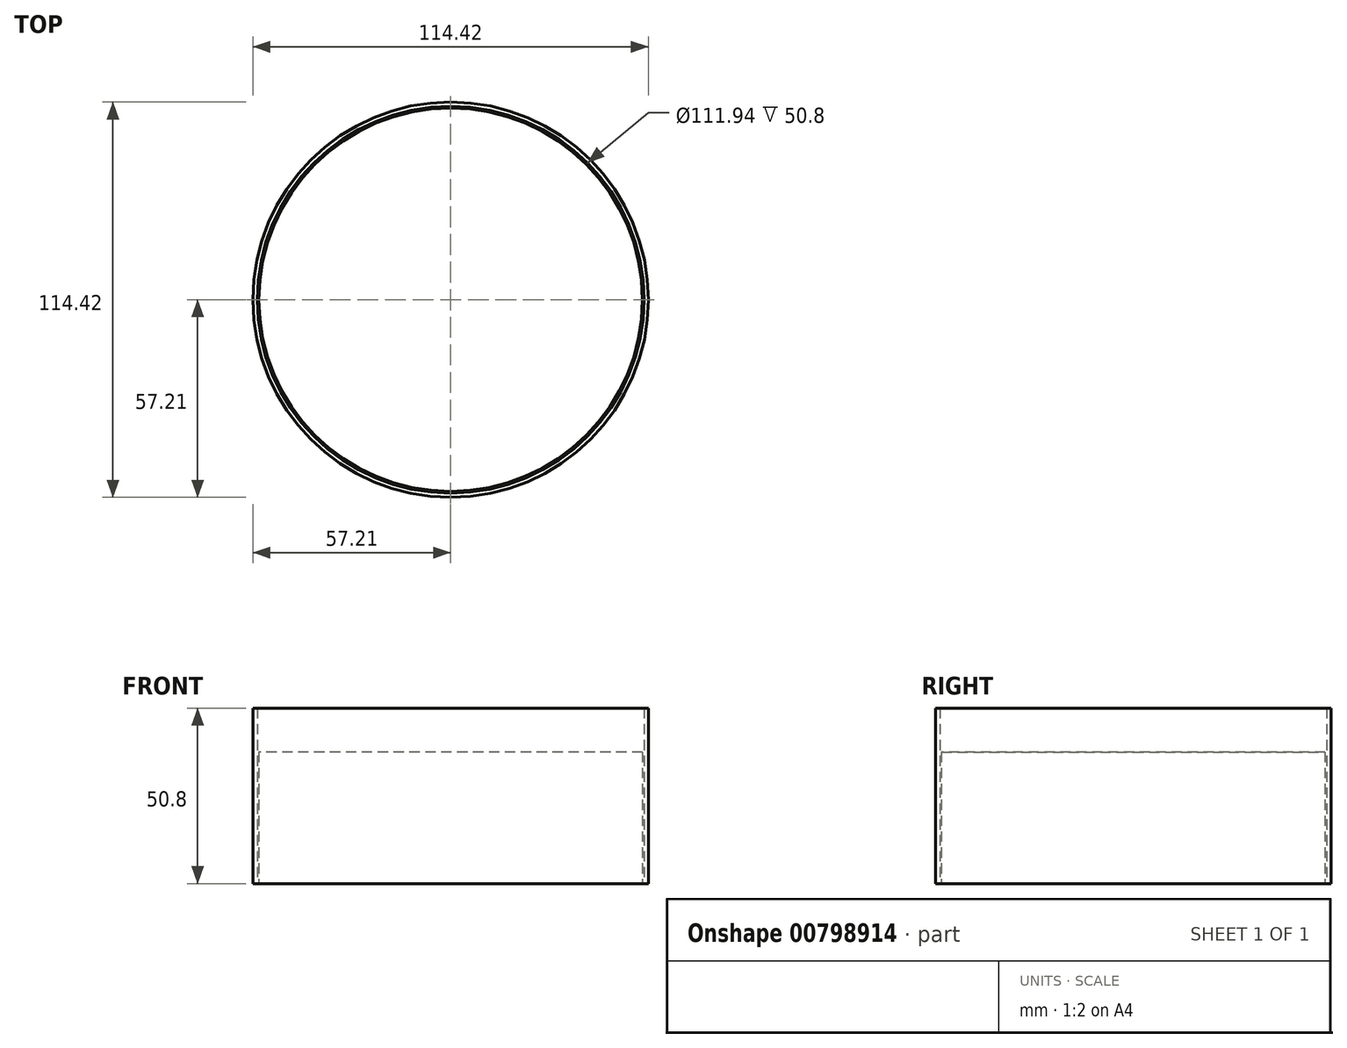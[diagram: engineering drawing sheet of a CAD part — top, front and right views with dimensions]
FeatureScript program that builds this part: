
annotation { "Feature Type Name" : "Feature", "Feature Type Description" : "" }
export const myFeature = defineFeature(function(context is Context, id is Id, definition is map)
    precondition{}
    {
        {
            var Q0;
            Q0=qCreatedBy(makeId("Top.planeOp"),FACE);
            var sketch = newSketch(context, id + "F0", { "sketchPlane" : qUnion([Q0])});
            skCircle(sketch, "E0", {"center": v(0, 0) * mm, "radius": 57.2 * mm});
            skCircle(sketch, "E1", {"center": v(0, 0) * mm, "radius": 55.97 * mm});
            skSolve(sketch);
        }
        {
            var Q0;
            Q0=makeQuery(id+"F0.imprint","IMPRINT",FACE,{"disambiguationData":[TD([[makeQuery(id+"F0.imprint","IMPRINT",EDGE,{"derivedFrom":sQuery(id+"F0.wireOp",EDGE,"E0")}),1.0]])]});
            extrude(context, id + "F1", {"entities" : qUnion([Q0]), "depth" : 50.8 * mm, "offsetDistance" : 25.4 * mm});
        }
        {
            var Q0;
            Q0=qCreatedBy(makeId("Top.planeOp"),FACE);
            var sketch = newSketch(context, id + "F2", { "sketchPlane" : qUnion([Q0])});
            skCircle(sketch, "E2", {"center": v(0, 0) * mm, "radius": 55.49 * mm});
            skSolve(sketch);
        }
        {
            var Q0;
            Q0=makeQuery(id+"F2.imprint","IMPRINT",FACE,{"disambiguationData":[TD([[makeQuery(id+"F2.imprint","IMPRINT",EDGE,{"derivedFrom":sQuery(id+"F2.wireOp",EDGE,"E2")}),1.0]])]});
            extrude(context, id + "F3", {"entities" : qUnion([Q0]), "depth" : 38.1 * mm, "offsetDistance" : 25.4 * mm});
        }
    });
